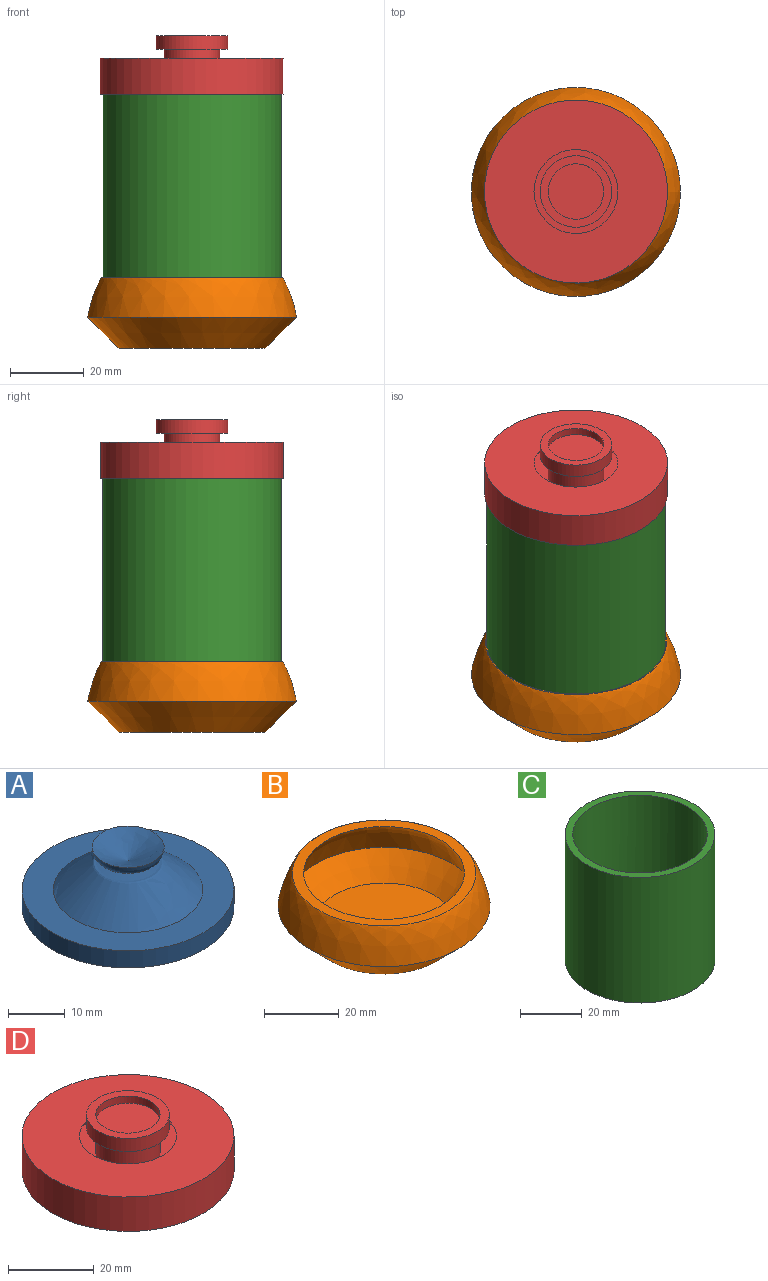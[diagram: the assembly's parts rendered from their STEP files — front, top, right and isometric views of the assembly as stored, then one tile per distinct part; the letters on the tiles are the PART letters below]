
ASSEMBLY  parts=4 mates=3
PART A: 6 faces, bbox 37.3x37.3x12.9 mm
  f0: revolved ~12.67x12.67mm, area 139.1mm2, adj f1
  f1: revolved ~12.67x12.67mm, area 166.9mm2, adj f0,f2
  f2: revolved ~26.23x26.23mm, area 655.4mm2, adj f1,f3
  f3: plane 37.25x37.25mm, normal (0,0,1), area 549.5mm2, adj f2,f4
  f4: cylinder r=18.63mm len=37.25mm, axis (0,0,1), area 430.1mm2, adj f3,f5
  f5: plane 37.25x37.25mm, normal (0,0,-1), area 1090mm2, adj f4
PART B: 7 faces, bbox 56.7x56.7x19.1 mm
  f0: revolved ~56.66x56.66mm, area 1910.8mm2, adj f1,f3
  f1: cone r=28.33mm half-angle=45.3deg, axis (0,0,1), area 1820.1mm2, adj f0,f2
  f2: plane 39.54x39.54mm, normal (0,0,-1), area 1228.1mm2, adj f1
  f3: plane 49.02x49.02mm, normal (0,0,1), area 437.2mm2, adj f0,f4
  f4: revolved ~51.29x51.29mm, area 1588.1mm2, adj f3,f5
  f5: cone r=26.57mm half-angle=45.3deg, axis (0,0,1), area 1354.5mm2, adj f4,f6
  f6: plane 37.49x37.49mm, normal (0,0,1), area 1103.6mm2, adj f5
PART C: 5 faces, bbox 48.5x48.5x49.7 mm
  f0: plane 48.49x48.49mm, normal (0,0,1), area 361.2mm2, adj f2,f4
  f1: plane 48.49x48.49mm, normal (0,0,-1), area 1846.9mm2, adj f2
  f2: cylinder r=24.25mm len=49.73mm, axis (0,0,1), area 7575.8mm2, adj f0,f1
  f3: plane 43.49x43.49mm, normal (0,0,1), area 1485.7mm2, adj f4
  f4: cylinder r=21.75mm len=47.23mm, axis (0,0,1), area 6453.1mm2, adj f0,f3
PART D: 11 faces, bbox 49.6x49.6x15.9 mm
  f0: plane 49.59x49.59mm, normal (0,0,1), area 1526mm2, adj f1,f10
  f1: cylinder r=24.8mm len=49.59mm, axis (0,0,-1), area 1532.9mm2, adj f0,f2
  f2: plane 49.59x49.59mm, normal (0,0,-1), area 1931.7mm2, adj f1
  f3: plane 15.02x15.02mm, normal (0,0,1), area 177.1mm2, adj f4
  f4: cylinder r=7.51mm len=15.02mm, axis (0,0,-1), area 95.8mm2, adj f3,f5
  f5: plane 19.37x19.37mm, normal (0,0,1), area 117.6mm2, adj f4,f6
  f6: cylinder r=9.69mm len=19.37mm, axis (0,0,-1), area 228.7mm2, adj f5,f7
  f7: plane 19.37x19.37mm, normal (0,0,-1), area 117.6mm2, adj f6,f8
  f8: cylinder r=7.51mm len=15.02mm, axis (0,0,-1), area 334.7mm2, adj f7,f9
  f9: plane 30.39x30.39mm, normal (0,0,1), area 548.3mm2, adj f8,f10
  f10: cone r=11.36mm half-angle=38.8deg, axis (0,0,-1), area 510.2mm2, adj f0,f9
PLACE A t=(35.62,46.53,50.86)mm
PLACE B t=(36.83,46.53,17.42)mm
PLACE C t=(63.4,46.53,-18.48)mm
PLACE D t=(-11.77,46.53,56.46)mm
MATE fastened B.f1 <-> C.f2  axis (0,0,1) through (-11.77,46.53,-18.48)mm
MATE fastened B.f1 <-> A.f4  axis (0,0,1) through (-11.77,46.53,-29.08)mm
MATE fastened D.f1 <-> C.f2  axis (0,0,-1) through (-11.77,46.53,31.25)mm
